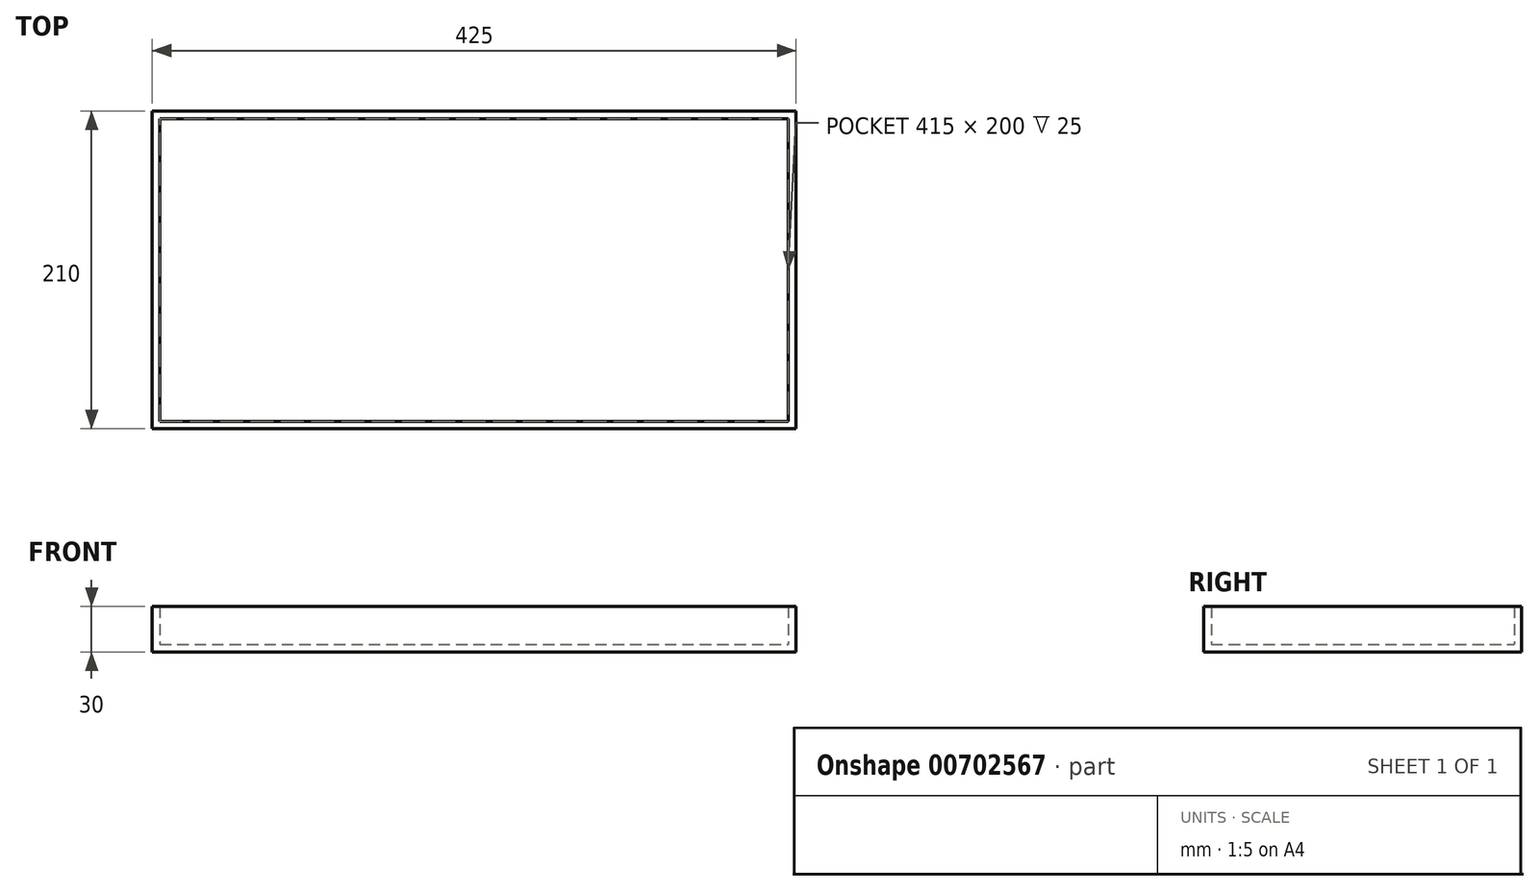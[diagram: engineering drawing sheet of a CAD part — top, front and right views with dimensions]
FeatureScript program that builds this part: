
annotation { "Feature Type Name" : "Feature", "Feature Type Description" : "" }
export const myFeature = defineFeature(function(context is Context, id is Id, definition is map)
    precondition{}
    {
        {
            var Q0;
            Q0=qCreatedBy(makeId("Top.planeOp"),FACE);
            var sketch = newSketch(context, id + "F0", { "sketchPlane" : qUnion([Q0])});
            skLineSegment(sketch, "E0.bottom", {"start": v(0, 0) * mm, "end": v(415, 0) * mm});
            skLineSegment(sketch, "E0.top", {"start": v(0, 200) * mm, "end": v(415, 200) * mm});
            skLineSegment(sketch, "E0.left", {"start": v(0, 0) * mm, "end": v(0, 200) * mm});
            skLineSegment(sketch, "E0.right", {"start": v(415, 0) * mm, "end": v(415, 200) * mm});
            skLineSegment(sketch, "E1.bottom", {"start": v(420, -5) * mm, "end": v(-5, -5) * mm});
            skLineSegment(sketch, "E1.top", {"start": v(420, 205) * mm, "end": v(-5, 205) * mm});
            skLineSegment(sketch, "E1.left", {"start": v(420, -5) * mm, "end": v(420, 205) * mm});
            skLineSegment(sketch, "E1.right", {"start": v(-5, -5) * mm, "end": v(-5, 205) * mm});
            skPoint(sketch, "E1.middle", {"position": v(207.5, 100) * mm});
            skPoint(sketch, "E1.middle.positionSnap0", {"position": v(415, 100) * mm});
            skPoint(sketch, "E1.middle.positionSnap1", {"position": v(207.5, 200) * mm});
            skPoint(sketch, "E1.centerSnap0", {"position": v(415, 100) * mm});
            skPoint(sketch, "E1.centerSnap1", {"position": v(207.5, 200) * mm});
            skSolve(sketch);
        }
        {
            var Q0;
            Q0=makeQuery(id+"F0.imprint","IMPRINT",FACE,{"disambiguationData":[TD([[makeQuery(id+"F0.imprint","IMPRINT",EDGE,{"derivedFrom":sQuery(id+"F0.wireOp",EDGE,"E0.bottom")}),-1.0]])]});
            extrude(context, id + "F1", {"entities" : qUnion([Q0]), "depth" : 30 * mm, "offsetDistance" : 25 * mm});
        }
        {
            var Q0;
            Q0=makeQuery(id+"F0.imprint","IMPRINT",FACE,{"disambiguationData":[TD([[makeQuery(id+"F0.imprint","IMPRINT",EDGE,{"derivedFrom":sQuery(id+"F0.wireOp",EDGE,"E0.bottom")}),1.0]])]});
            extrude(context, id + "F2", {"entities" : qUnion([Q0]), "operationType" : NewBodyOperationType.ADD, "depth" : 5 * mm, "offsetDistance" : 25 * mm});
        }
    });
